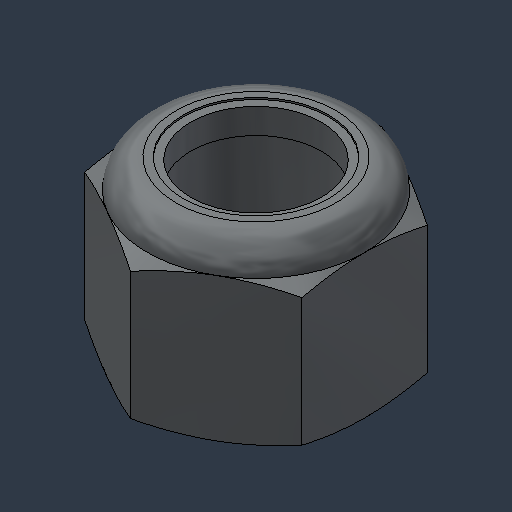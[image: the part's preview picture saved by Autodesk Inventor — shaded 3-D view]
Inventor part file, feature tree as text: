
AUTODESK INVENTOR PART (.ipt)
format: ipt  version: 2024.3 (Build 283343000, 343)  size: 185,856 bytes
history: native  units: mm (DEFAULTED — no unit token found)
features: other x1, revolve x1
ambient origin geometry x8: Origin, YZ Plane, XZ Plane, XY Plane, X Axis, Y Axis, Z Axis, Center Point
bodies: Solid1 (feature_tree), Solid2 (feature_tree)
feature tree (2):
  other  "Cut-Revolve4"
  revolve  "Revolve2"  [1 undecoded]
note: 1 required parameter value undecoded (feature->parameter linkage not recoverable at this tier; creation-order binding heuristic only, values carry confidence <= 0.55)
